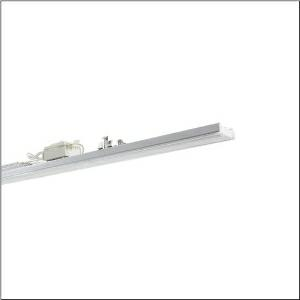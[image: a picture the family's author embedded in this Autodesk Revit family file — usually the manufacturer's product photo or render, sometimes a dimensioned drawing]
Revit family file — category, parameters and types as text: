
# Revit family: licross_r__21_recessed_mo_52te12dn495g_e9f1
name_source: partatom
category: Lighting Fixtures
units: mm (PartAtom-declared; Revit-internal decimal feet)

## family parameters
Cut with Voids When Loaded = No
Host = Face
Light Source = No
Part Type = Normal
Room Calculation Point = No
Round Connector Dimension = Use Diameter
Shared = No

## types (1)
- --- (1 x LED, 9520 lm, 53.3 W, 4000K)
    Apparent Load = 53 VA
    CIE Flux Codes = 72 92 99 100 100
    Color Rendering = 80
    Color Temperature = 4000K
    Default Elevation = 1800 mm
    Description = Licross® 21 Recessed MO, luminaire insert, of sheet steel, galvanised, coil coated, white, length: 1.500mm, width: 66mm, height: 67mm, LED rated luminous flux: 9.520lm, light colour: 840, control gear: DALI 2, with plug, 5-pole, with phase selection, mains connection: 220..240V, AC, 50/60Hz, rated input power: 53W, halogen-free wiring, primary optical cover: cover, of PMMA, light emission: direct distribution, primary light characteristic: symmetric, protection rating (complete): IP54, insulation class (complete): insulation class I (protective earthing), certification: CE, ENEC, VDE, UKCA, protection symbol: D if used in an environment with non-conductive dust loads with corresponding accessories, impact resistance: IK06, permissible ambient temperature for indoor applications: -25..+35°C, corresponds to IFS (International Featured Standards) requirements for safety and quality in the food industry, reducing of maximum allowable ambient temperature of 5°C with ceiling mounting, LABS conformity tested according to VDMA 24364:2018-05, packaging unit: 1 piece
    Height = 58 mm
    Lamp = 1 x LED
    Lamp Light Flux = 9520 lm
    Lamp Power = 53.3 W
    Lamp count = 1
    Length = 1500 mm
    Luminous efficacy = 179 lm/W
    Manufacturer = Siteco
    ModVariant = No
    Model = 52TE12DN495G
    Mounting Place = Ceiling
    Mounting Type = Pendant
    Number of Poles = 1
    OnlyDefault = Yes
    Power Factor = 1
    Product Name = Licross® 21 Recessed MO
    Product group = luminaire insert
    ProductGroupID = 902
    Protection Class = Protection class I
    Protection Degree = IP 54
    RLX_Detail_Level = 1
    RLX_Emergency_Light_Flux = 0 lm
    RLX_Emergency_Type = 0
    RLX_Emergency_Type_DB = No
    RlxData = <blob elided: 24565 chars, md5=05b00c25>
    Socket = socket
    Standby Power = 0 W
    System Light Flux = 9520 lm
    System Power = 53 W
    Type Comments = factory setting: luminous flux: 100 % | dim-lin: 254 | 359 mA
    Type Image = l_1296930.jpg
    URL = http://relux.com
    VarID = @adj_079776
    Voltage = 0 V
    Weight = 0.00 kg
    Width = 66 mm

## geometry (parser evidence)
native form markers: Blend x4, Sweep x12
no freeform markers — native parametric forms only
